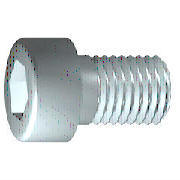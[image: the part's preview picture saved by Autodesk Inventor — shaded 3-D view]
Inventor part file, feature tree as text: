
AUTODESK INVENTOR PART (.ipt)
format: ipt  version: 2025.1 (Build 291241000, 241)  size: 195,072 bytes
history: native  units: mm (DEFAULTED — no unit token found)
features: other x1, extrude x1, plane x1, fillet x1
ambient origin geometry x7: Origin, YZ Plane, XY Plane, X Axis, Y Axis, Z Axis, Center Point
bodies: Solid1 (feature_tree)
feature tree (4):
  other  "Corps"
  extrude  "Rainure"  Depth=10.75mm
  plane  "Work Plane1"
  fillet  "Fillet2"  Radius=0.306825mm
